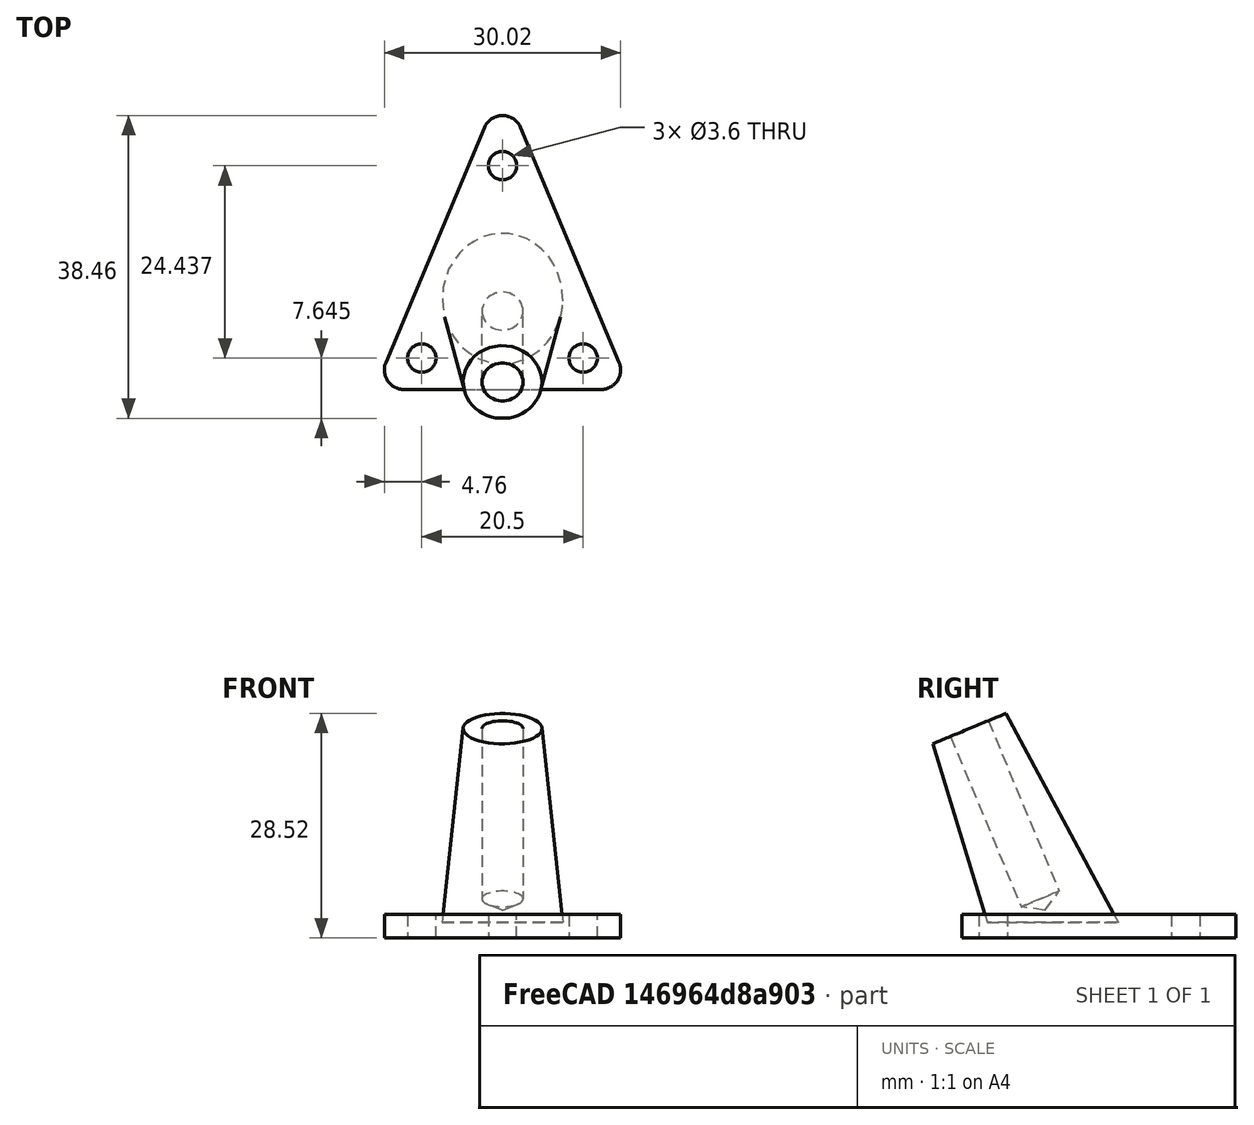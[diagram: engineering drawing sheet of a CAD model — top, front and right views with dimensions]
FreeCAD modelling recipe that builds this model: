
FCSTD DOCUMENT  (FreeCAD 0.18R4 (GitTag))
Label: landing_gear_base
License: All rights reserved
LicenseURL: http://en.wikipedia.org/wiki/All_rights_reserved
objects: PartDesign::Body×2, Sketcher::SketchObject×1, PartDesign::Pad×1, Part::Cone×1, PartDesign::FeatureBase×1, PartDesign::SubtractiveBox×1, PartDesign::Hole×1, Mesh::Feature×1
note: 11 computed .brp shape members not serialized (recipe doc carries the construction recipe); baked Part::Feature solids carry a one-line shape summary decoded from their .brp

FEATURE [Sketcher::SketchObject] Sketch
  MapMode = 5
  Support = -> [XY_Plane]
  sketch-geometry (9):
    g0: LineSegment StartX=-12.5058 StartY=-3.4946 StartZ=0 EndX=12.5058 EndY=-3.4946 EndZ=0
    g1: LineSegment StartX=-2.30542 StartY=29.7879 StartZ=0 EndX=-14.8112 EndY=-0.0276164 EndZ=0
    g2: LineSegment StartX=2.30542 StartY=29.7879 StartZ=0 EndX=14.8112 EndY=-0.0276164 EndZ=0
    g3: ArcOfCircle CenterX=12.5058 CenterY=-0.994597 CenterZ=0 NormalX=0 NormalY=0 NormalZ=1 AngleXU=0 Radius=2.5 StartAngle=4.71239 EndAngle=6.68034
    g4: ArcOfCircle CenterX=-12.5058 CenterY=-0.994597 CenterZ=0 NormalX=0 NormalY=0 NormalZ=1 AngleXU=0 Radius=2.5 StartAngle=2.74444 EndAngle=4.71239
    g5: ArcOfCircle CenterX=8e-16 CenterY=28.8209 CenterZ=0 NormalX=0 NormalY=0 NormalZ=1 AngleXU=0 Radius=2.5 StartAngle=0.397151 EndAngle=2.74444
    g6: Circle CenterX=10.25 CenterY=0.505403 CenterZ=0 NormalX=0 NormalY=0 NormalZ=1 AngleXU=0 Radius=1.8
    g7: Circle CenterX=-10.25 CenterY=0.505403 CenterZ=0 NormalX=0 NormalY=0 NormalZ=1 AngleXU=0 Radius=1.8
    g8: Circle CenterX=2.9e-15 CenterY=24.9428 CenterZ=0 NormalX=0 NormalY=0 NormalZ=1 AngleXU=0 Radius=1.8
  constraints (23):
    c: Horizontal(g0)
    c: Tangent(g0,g3) = -1.5708
    c: Tangent(g2,g3) = 1.5708
    c: Tangent(g0,g4) = -1.5708
    c: Tangent(g1,g4) = -1.5708
    c: Tangent(g1,g5) = -1.5708
    c: Tangent(g2,g5) = 1.5708
    c: Radius(g3) = 2.5
    c: Equal(g3,g5)
    c: Equal(g5,g4)
    c: Distance(g7,g0) = 4
    c: Distance(g6,g0) = 4
    c: Distance(g6,g2) = 4
    c: Distance(g7,g1) = 4
    c: Distance(g8,g2) = 4
    c: Distance(g8,g1) = 4
    c: Distance(g7,g6) = 20.5
    c: Distance(g6,g8) = 26.5
    c: Distance(g7,g8) = 26.5
    c: DistanceX(g-1,g6) = 10.25
    c: Radius(g7) = 1.8
    c: Equal(g7,g6)
    c: Equal(g7,g8)
FEATURE [PartDesign::Pad] Pad
  Length = 3
  Length2 = 100
  Profile = -> Sketch
  Type = 0
FEATURE [PartDesign::Body] Body  label="Plate"
  Group = -> [Sketch,Pad]
  Origin = -> Origin
  Tip = -> Pad
FEATURE [Part::Cone] Cone
  Angle = 360
  AttacherType = Attacher::AttachEngine3D
  Height = 30
  Placement = pos=(0,9,9) rot=(1,0,0;0.392699rad)
  Radius1 = 8
  Radius2 = 5
FEATURE [PartDesign::FeatureBase] BaseFeature
  BaseFeature = -> Cone
FEATURE [PartDesign::SubtractiveBox] Box
  AttacherType = Attacher::AttachEngine3D
  AttachmentOffset = pos=(-11,0.3,-9) rot=(0,0,-1;0.392699rad)
  BaseFeature = -> BaseFeature
  Height = 18
  Length = 20
  MapMode = 5
  Placement = pos=(-9,-11,0.3) rot=(0.485653,0.726831,0.485653;1.88458rad)
  Support = -> [YZ_Plane001]
  Width = 7
FEATURE [PartDesign::Hole] Hole
  BaseFeature = -> Box
  Depth = 25
  DepthType = 0
  Diameter = 5.2
  DrillPoint = 1
  DrillPointAngle = 118
  HoleCutCountersinkAngle = 90
  HoleCutDepth = 0
  HoleCutDiameter = 0
  HoleCutType = 0
  ModelActualThread = false
  Placement = pos=(-9,-11,0.3) rot=(0.485653,0.726831,0.485653;1.88458rad)
  Profile = -> Box [Face3]
  Tapered = false
  TaperedAngle = 90
  ThreadAngle = 0
  ThreadClass = 0
  ThreadCutOffInner = 0
  ThreadCutOffOuter = 0
  ThreadDirection = 0
  ThreadFit = 0
  ThreadPitch = 0
  ThreadSize = 0
  ThreadType = 0
  Threaded = false
FEATURE [PartDesign::Body] Body001  label="Cone001"
  BaseFeature = -> Cone
  Group = -> [BaseFeature,Box,Hole]
  Origin = -> Origin001
  Placement = pos=(0,9,-1.1) rot=(1,0,0;0.394444rad)
  Tip = -> Hole
FEATURE [Mesh::Feature] Mesh002  label="landing_gear_base"
